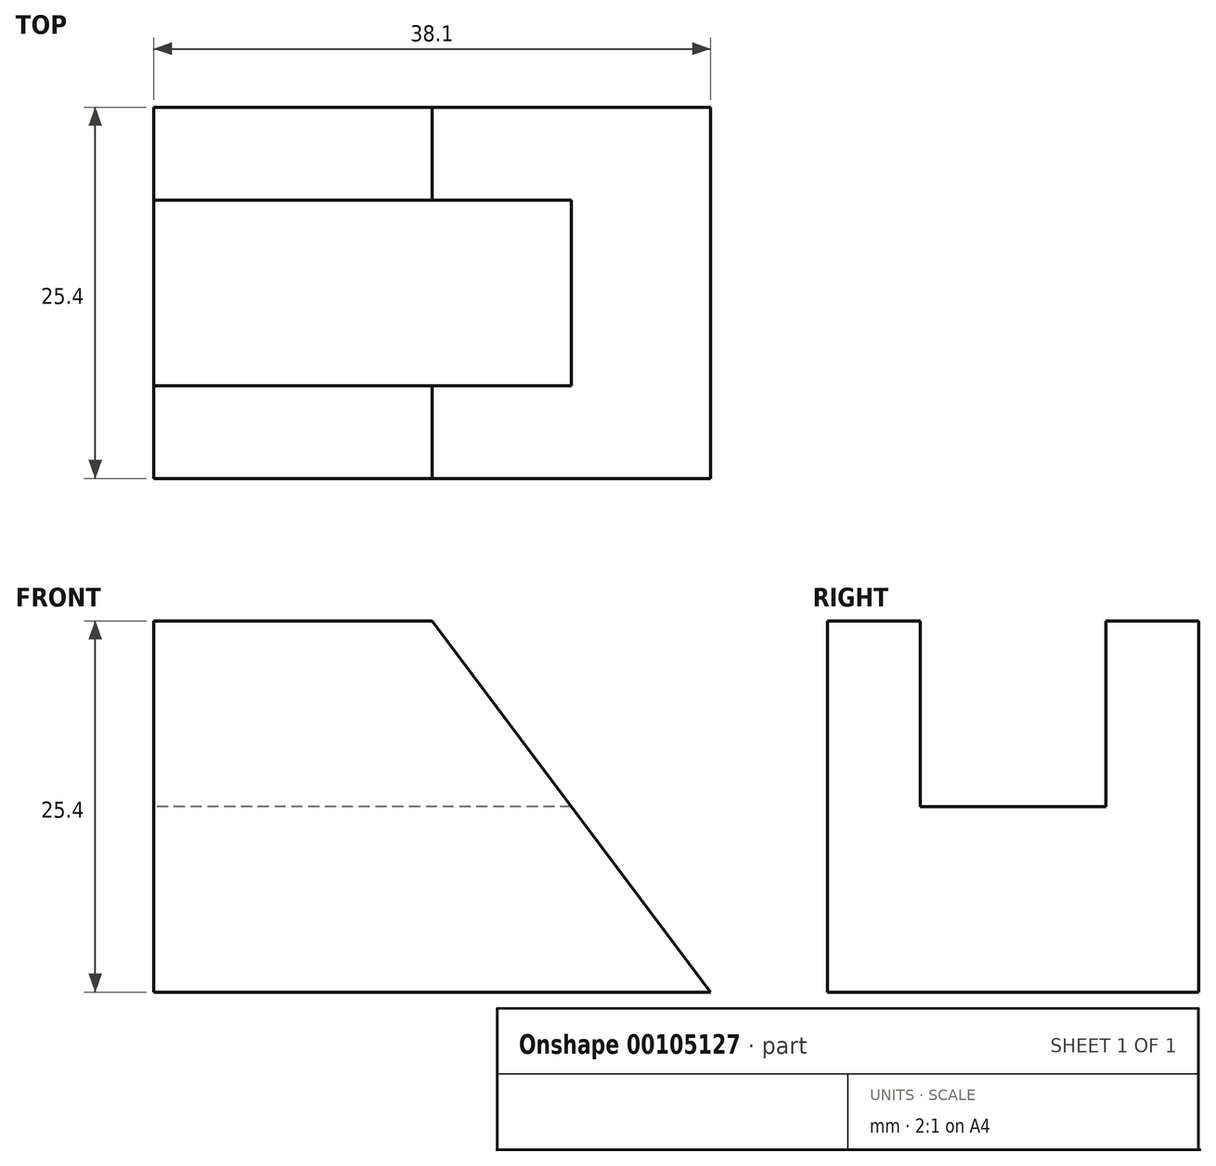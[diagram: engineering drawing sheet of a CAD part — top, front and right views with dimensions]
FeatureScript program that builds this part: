
annotation { "Feature Type Name" : "Feature", "Feature Type Description" : "" }
export const myFeature = defineFeature(function(context is Context, id is Id, definition is map)
    precondition{}
    {
        {
            var Q0;
            Q0=qCreatedBy(makeId("Front.planeOp"),FACE);
            var sketch = newSketch(context, id + "F0", { "sketchPlane" : qUnion([Q0])});
            skLineSegment(sketch, "E0", {"start": v(0, 0) * mm, "end": v(0, 25.4) * mm});
            skLineSegment(sketch, "E1", {"start": v(0, 25.4) * mm, "end": v(19.05, 25.4) * mm});
            skLineSegment(sketch, "E2", {"start": v(19.05, 25.4) * mm, "end": v(38.1, 0) * mm});
            skLineSegment(sketch, "E3", {"start": v(38.1, 0) * mm, "end": v(0, 0) * mm});
            skSolve(sketch);
        }
        {
            var Q0;
            Q0 = qSketchRegion(id + "F0", true);
            extrude(context, id + "F1", {"entities" : qUnion([Q0]), "oppositeDirection" : true, "depth" : 25.4 * mm});
        }
        {
            var Q0;
            Q0=makeQuery(id+"F1.opExtrude","SWEPT_FACE",FACE,{"disambiguationData":[OSD([sQuery(id+"F0.wireOp",EDGE,"E0")])]});
            var sketch = newSketch(context, id + "F2", { "sketchPlane" : qUnion([Q0])});
            skLineSegment(sketch, "E4", {"start": v(-19.05, 25.4) * mm, "end": v(-19.05, 12.7) * mm});
            skLineSegment(sketch, "E5", {"start": v(-19.05, 12.7) * mm, "end": v(-6.35, 12.7) * mm});
            skLineSegment(sketch, "E6", {"start": v(-6.35, 12.7) * mm, "end": v(-6.35, 25.4) * mm});
            skSolve(sketch);
        }
        {
            var Q0;
            {var subQ0=sQuery(id+"F2.wireOp",EDGE,"E4");Q0=makeQuery(id+"F2.imprint","IMPRINT",FACE,{"disambiguationData":[TD([[makeQuery(id+"F2.imprint","IMPRINT",EDGE,{"derivedFrom":subQ0}),1.0]])]});}
            extrude(context, id + "F3", {"entities" : qUnion([Q0]), "operationType" : NewBodyOperationType.REMOVE, "endBound" : BoundingType.THROUGH_ALL, "oppositeDirection" : true, "depth" : 25.4 * mm});
        }
    });
